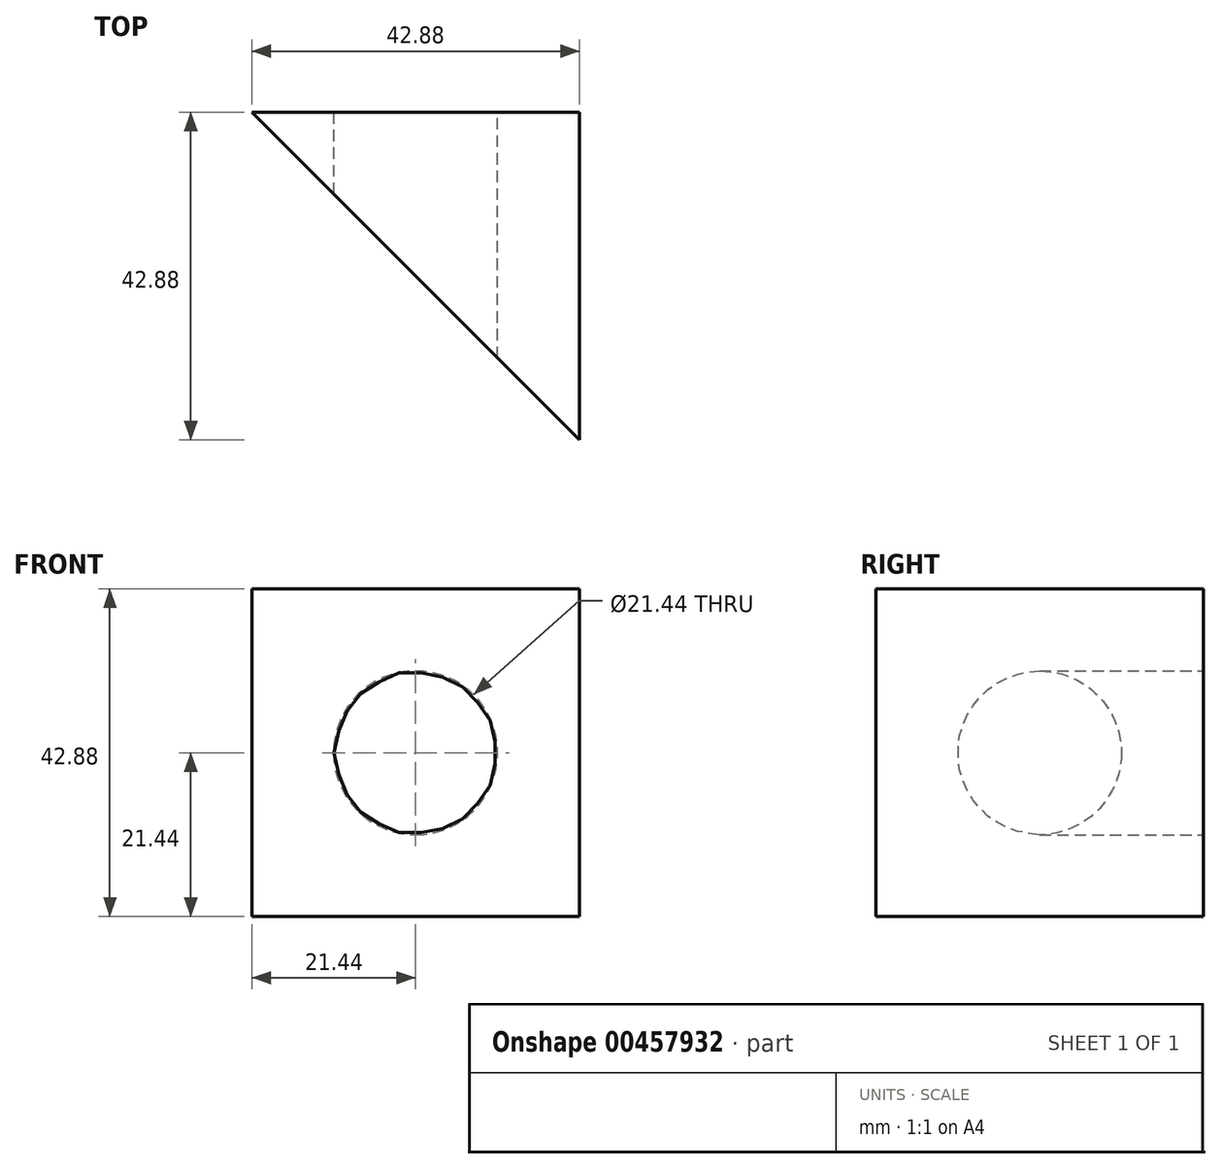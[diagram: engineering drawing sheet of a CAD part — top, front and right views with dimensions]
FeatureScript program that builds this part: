
annotation { "Feature Type Name" : "Feature", "Feature Type Description" : "" }
export const myFeature = defineFeature(function(context is Context, id is Id, definition is map)
    precondition{}
    {
        {
            var Q0;
            Q0=qCreatedBy(makeId("Front.planeOp"),FACE);
            var sketch = newSketch(context, id + "F0", { "sketchPlane" : qUnion([Q0])});
            skLineSegment(sketch, "E0.bottom", {"start": v(-21.44, 21.44) * mm, "end": v(21.44, 21.44) * mm});
            skLineSegment(sketch, "E0.top", {"start": v(-21.44, -21.44) * mm, "end": v(21.44, -21.44) * mm});
            skLineSegment(sketch, "E0.left", {"start": v(-21.44, 21.44) * mm, "end": v(-21.44, -21.44) * mm});
            skLineSegment(sketch, "E0.right", {"start": v(21.44, 21.44) * mm, "end": v(21.44, -21.44) * mm});
            skPoint(sketch, "E0.middle", {"position": v(0, 0) * mm});
            skCircle(sketch, "E1", {"center": v(0, 0) * mm, "radius": 10.72 * mm});
            skSolve(sketch);
        }
        {
            var Q0;
            Q0=makeQuery(id+"F0.imprint","IMPRINT",FACE,{"disambiguationData":[TD([[makeQuery(id+"F0.imprint","IMPRINT",EDGE,{"derivedFrom":sQuery(id+"F0.wireOp",EDGE,"E0.bottom")}),-1.0]])]});
            extrude(context, id + "F1", {"entities" : qUnion([Q0]), "depth" : 42.88 * mm, "offsetDistance" : 25.4 * mm});
        }
        {
            var Q0;
            Q0=makeQuery(id+"F1.opExtrude","SWEPT_FACE",FACE,{"disambiguationData":[OSD([sQuery(id+"F0.wireOp",EDGE,"E0.bottom")])]});
            var sketch = newSketch(context, id + "F2", { "sketchPlane" : qUnion([Q0])});
            skLineSegment(sketch, "E2", {"start": v(-21.44, 0) * mm, "end": v(21.44, -42.88) * mm});
            skSolve(sketch);
        }
        {
            var Q0;
            Q0=makeQuery(id+"F2.imprint","IMPRINT",FACE,{"disambiguationData":[TD([[makeQuery(id+"F2.imprint","IMPRINT",EDGE,{"derivedFrom":sQuery(id+"F2.wireOp",EDGE,"E2")}),-1.0]])]});
            extrude(context, id + "F3", {"entities" : qUnion([Q0]), "operationType" : NewBodyOperationType.REMOVE, "oppositeDirection" : true, "depth" : 42.88 * mm, "offsetDistance" : 25.4 * mm});
        }
    });
